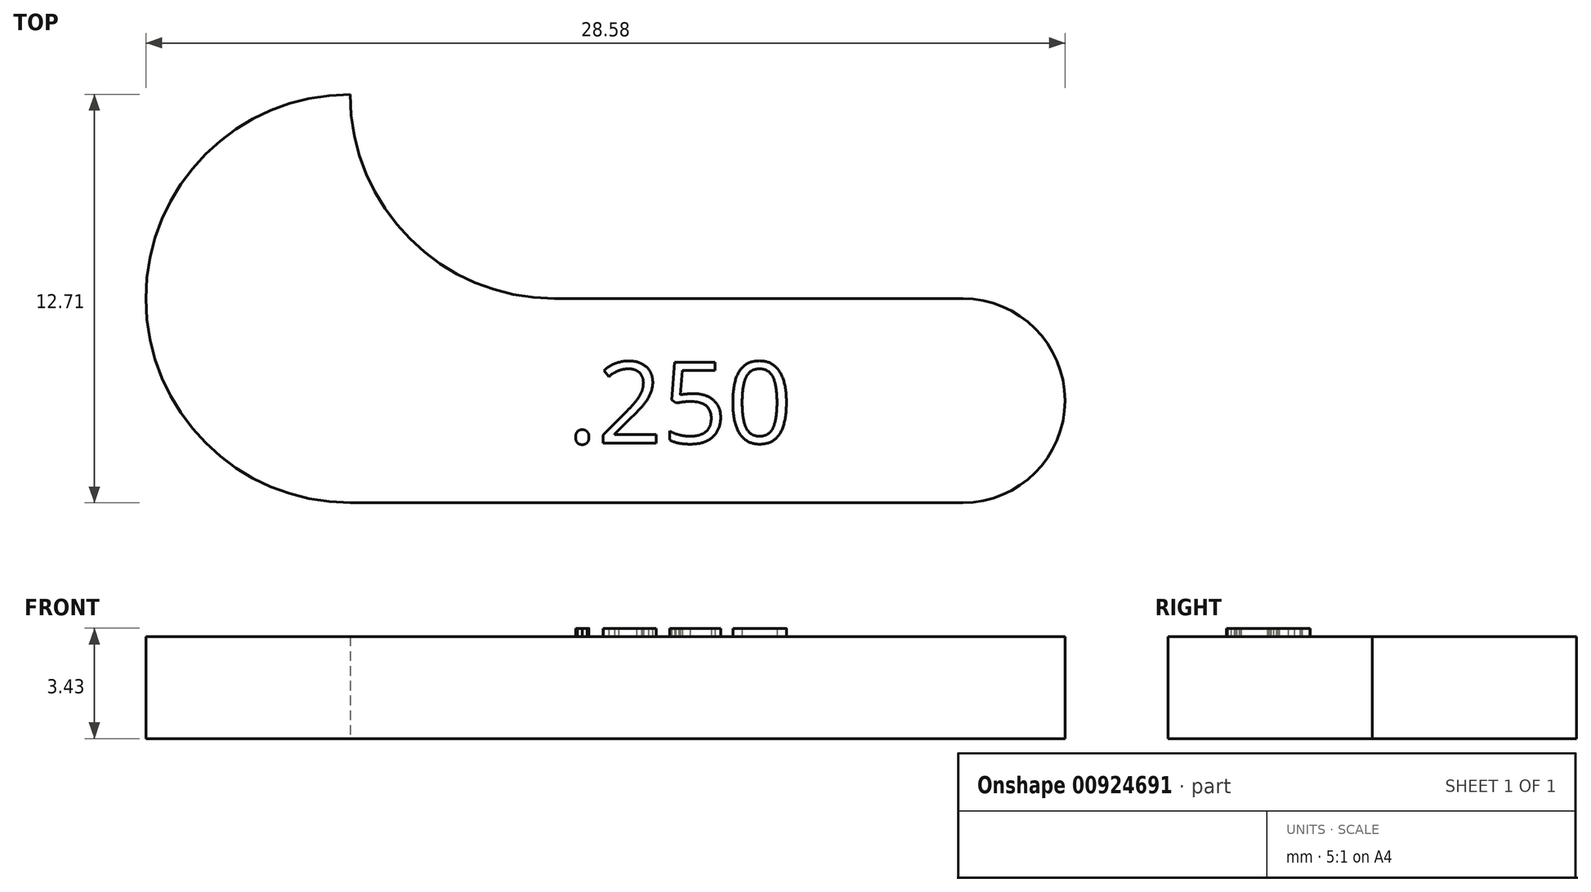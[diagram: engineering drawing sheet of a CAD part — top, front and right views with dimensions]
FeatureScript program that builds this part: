
annotation { "Feature Type Name" : "Feature", "Feature Type Description" : "" }
export const myFeature = defineFeature(function(context is Context, id is Id, definition is map)
    precondition{}
    {
        {
            var Q0;
            Q0=qCreatedBy(makeId("Top.planeOp"),FACE);
            var sketch = newSketch(context, id + "F0", { "sketchPlane" : qUnion([Q0])});
            skArc(sketch, "E0", {"start": v(-19.05, 9.53) * mm, "mid": v(-25.4, 3.18) * mm, "end": v(-19.05, -3.17) * mm});
            skLineSegment(sketch, "E1", {"start": v(-19.05, -3.17) * mm, "end": v(0, -3.18) * mm});
            skArc(sketch, "E2", {"start": v(0, -3.18) * mm, "mid": v(3.18, 0) * mm, "end": v(0, 3.18) * mm});
            skLineSegment(sketch, "E3", {"start": v(0, 3.17) * mm, "end": v(-12.7, 3.17) * mm});
            skArc(sketch, "E4", {"start": v(-19.05, 9.53) * mm, "mid": v(-17.2, 5.03) * mm, "end": v(-12.7, 3.17) * mm});
            skSolve(sketch);
        }
        {
            var Q0;
            Q0 = qSketchRegion(id + "F0", true);
            extrude(context, id + "F1", {"entities" : qUnion([Q0]), "depth" : 3.17 * mm, "offsetDistance" : 25.4 * mm});
        }
        {
            var Q0;
            Q0=makeQuery(id+"F1.opExtrude","CAP_FACE",FACE,{"disambiguationData":[OSD([sQuery(id+"F0.wireOp",EDGE,"E0"),sQuery(id+"F0.wireOp",EDGE,"E1"),sQuery(id+"F0.wireOp",EDGE,"E2"),sQuery(id+"F0.wireOp",EDGE,"E3"),sQuery(id+"F0.wireOp",EDGE,"E4")])],"isStart":false});
            var sketch = newSketch(context, id + "F2", { "sketchPlane" : qUnion([Q0])});
            skText(sketch, "E5", { "text": ".250\n", "fontName": "OpenSans-Regular.ttf"});
            const initialGuessF2  = {"E5": [-0.0123, -0.00132, 1, 0, 0.00254]};
            skSetInitialGuess(sketch, initialGuessF2);
            skSolve(sketch);
        }
        {
            var Q0;
            Q0 = qSketchRegion(id + "F2", true);
            extrude(context, id + "F3", {"entities" : qUnion([Q0]), "operationType" : NewBodyOperationType.ADD, "depth" : 0.25 * mm, "offsetDistance" : 25.4 * mm});
        }
    });
